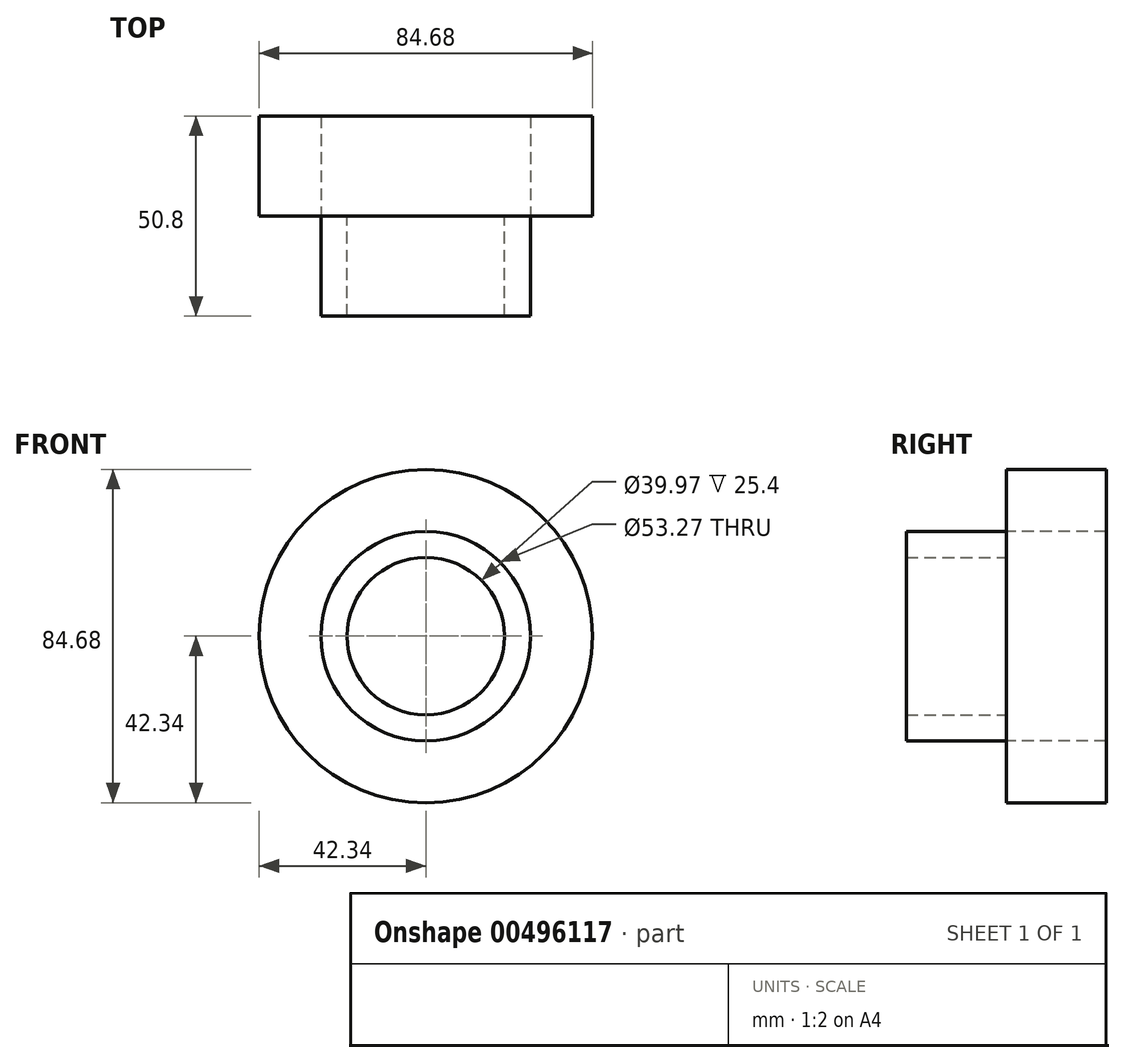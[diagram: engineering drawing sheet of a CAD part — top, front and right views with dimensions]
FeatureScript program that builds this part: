
annotation { "Feature Type Name" : "Feature", "Feature Type Description" : "" }
export const myFeature = defineFeature(function(context is Context, id is Id, definition is map)
    precondition{}
    {
        {
            var Q0;
            Q0=qCreatedBy(makeId("Front.planeOp"),FACE);
            var sketch = newSketch(context, id + "F0", { "sketchPlane" : qUnion([Q0])});
            skCircle(sketch, "E0", {"center": v(0, 0) * mm, "radius": 26.63 * mm});
            skCircle(sketch, "E1", {"center": v(0, 0) * mm, "radius": 19.98 * mm});
            skCircle(sketch, "E2", {"center": v(0, 0) * mm, "radius": 42.34 * mm});
            skSolve(sketch);
        }
        {
            var Q0;
            Q0=makeQuery(id+"F0.imprint","IMPRINT",FACE,{"disambiguationData":[TD([[makeQuery(id+"F0.imprint","IMPRINT",EDGE,{"derivedFrom":sQuery(id+"F0.wireOp",EDGE,"E0")}),1.0]])]});
            extrude(context, id + "F1", {"entities" : qUnion([Q0]), "depth" : 25.4 * mm});
        }
        {
            var Q0;
            Q0=makeQuery(id+"F0.imprint","IMPRINT",FACE,{"disambiguationData":[TD([[makeQuery(id+"F0.imprint","IMPRINT",EDGE,{"derivedFrom":sQuery(id+"F0.wireOp",EDGE,"E0")}),-1.0]])]});
            extrude(context, id + "F2", {"entities" : qUnion([Q0]), "operationType" : NewBodyOperationType.ADD, "oppositeDirection" : true, "depth" : 25.4 * mm});
        }
    });
